# Revit family: Hose-Stream-Rated_Smoke-Fire-Curtain_DoorSystems_DSI-HS10B-Single-Roller-Headbox
name_source: partatom
category: Doors
units: mm (PartAtom-declared; Revit-internal decimal feet)

## family parameters
Always vertical = Yes
Cut with Voids When Loaded = No
Host = Wall
OmniClass Number = 23.30.10.21.11.11
OmniClass Title = Rolling Fire Doors
Room Calculation Point = No
Shared = No

## types (2) — shared parameters
Analytic Construction = <None>
CAD Details = https://www.arcat.com
CurtainDrop_Viz = Yes
Define Thermal Properties by = Schematic Type
Description = Hose Stream Rated Smoke and Fire Curtain
Fire Performance = UL 10B
Fire Rating = 1, 2, 3
Frame Width = 0' - 6"
FrameDepth = 0' - 2"
Keynote = 08 33 44
Manufacturer = Door Systems
Model = DSI-HS10B
Product Page URL = https://www.arcat.com
Rough Height = 0' - 0"
Rough Width = 0' - 0"
Specification = https://www.arcat.com
URL = https://www.doorsysinc.com
Wall Closure = By host

## per-type parameters (varying)
| type | HeadBox_Depth | HeadBox_Height |
| 9" x 9" Head-box #1 | 0' - 9" | 0' - 9" |
| 10" x 10" Head-box #2 | 0' - 10" | 0' - 10" |

## geometry (parser evidence)
native form markers: Sweep x2
no freeform markers — native parametric forms only
